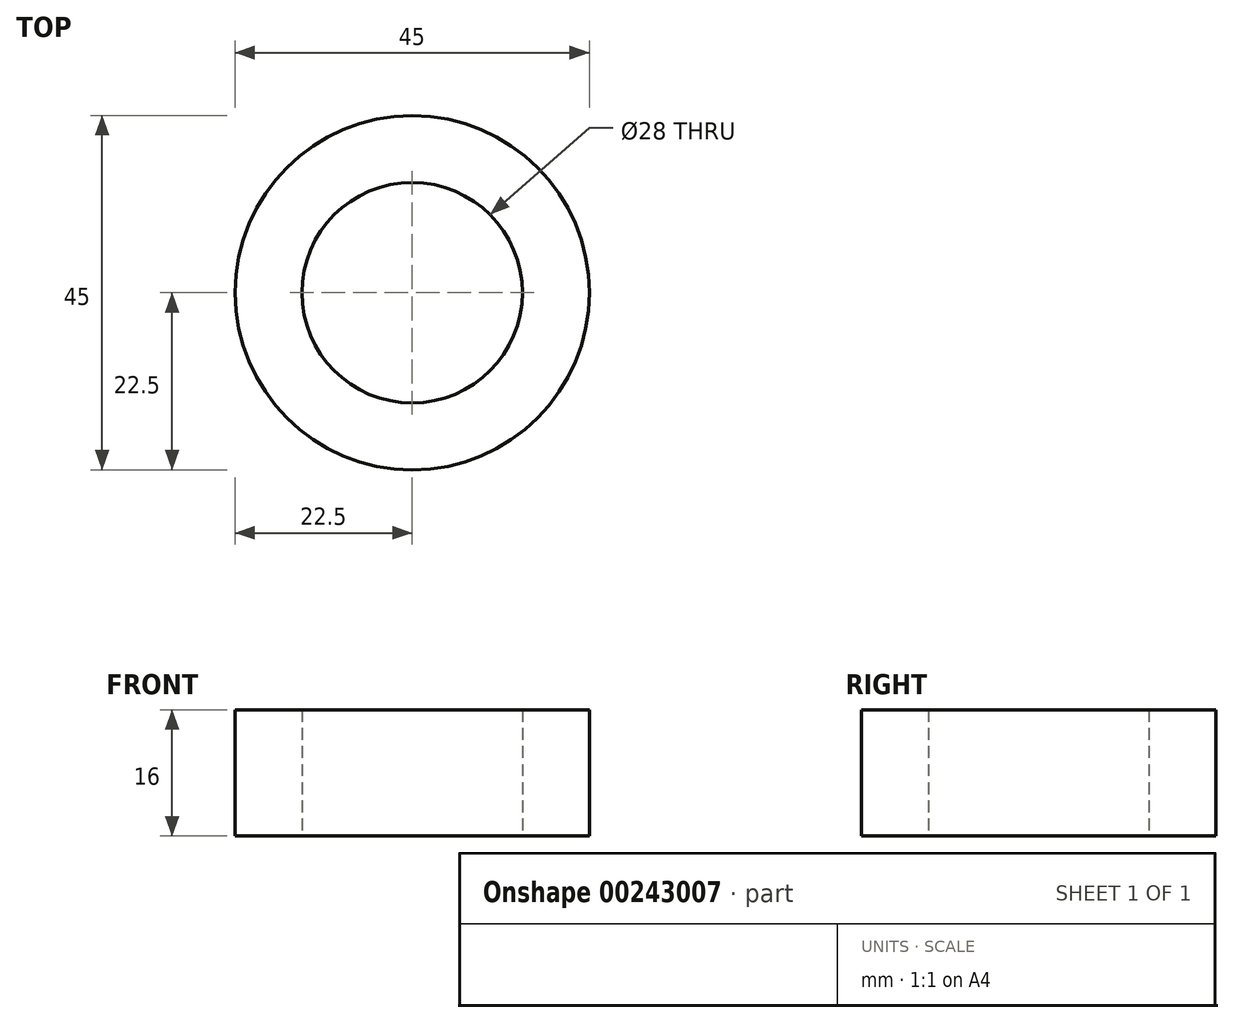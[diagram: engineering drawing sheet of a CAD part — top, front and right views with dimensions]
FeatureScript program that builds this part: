
annotation { "Feature Type Name" : "Feature", "Feature Type Description" : "" }
export const myFeature = defineFeature(function(context is Context, id is Id, definition is map)
    precondition{}
    {
        {
            var Q0;
            Q0=qCreatedBy(makeId("Top.planeOp"),FACE);
            var sketch = newSketch(context, id + "F0", { "sketchPlane" : qUnion([Q0])});
            skCircle(sketch, "E0", {"center": v(0, 0) * mm, "radius": 22.5 * mm});
            skCircle(sketch, "E1", {"center": v(0, 0) * mm, "radius": 14 * mm});
            skSolve(sketch);
        }
        {
            var Q0;
            Q0 = qSketchRegion(id + "F0", true);
            extrude(context, id + "F1", {"entities" : qUnion([Q0]), "depth" : 16 * mm});
        }
    });
